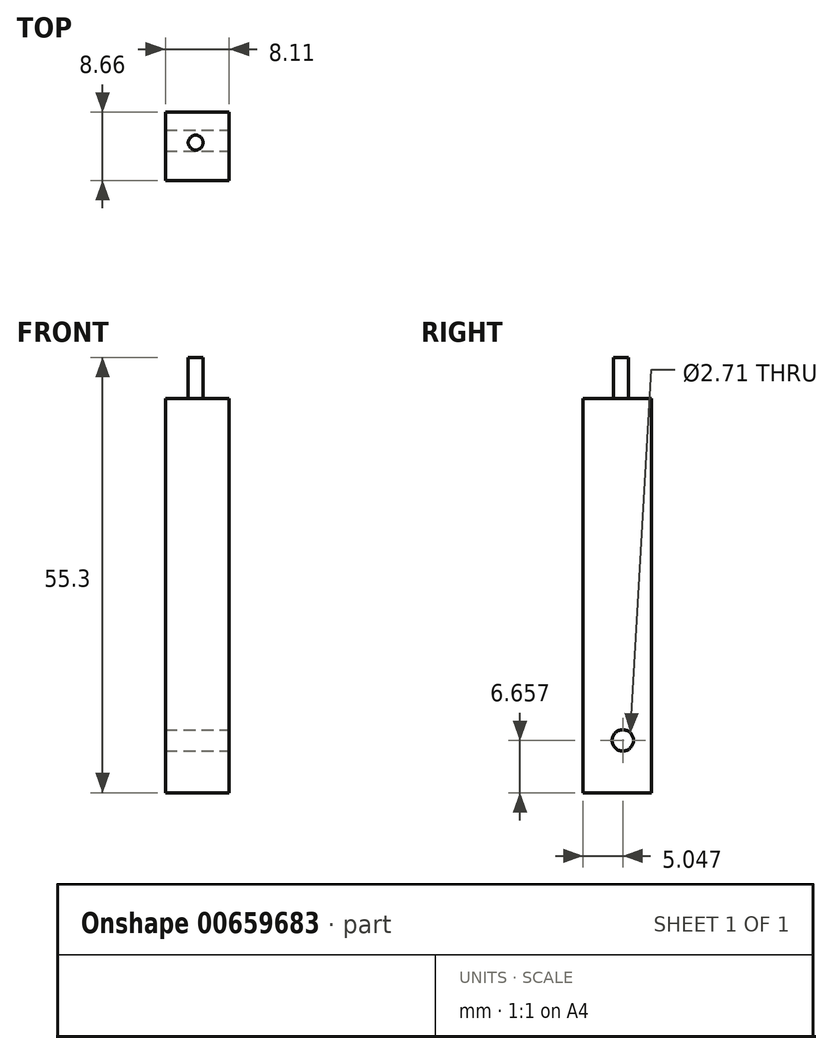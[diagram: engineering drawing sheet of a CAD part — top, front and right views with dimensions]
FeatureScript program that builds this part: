
annotation { "Feature Type Name" : "Feature", "Feature Type Description" : "" }
export const myFeature = defineFeature(function(context is Context, id is Id, definition is map)
    precondition{}
    {
        {
            var Q0;
            Q0=qCreatedBy(makeId("Top.planeOp"),FACE);
            var sketch = newSketch(context, id + "F0", { "sketchPlane" : qUnion([Q0])});
            skLineSegment(sketch, "E0.bottom", {"start": v(0, 0) * mm, "end": v(8.11, 0) * mm});
            skLineSegment(sketch, "E0.top", {"start": v(0, -8.66) * mm, "end": v(8.11, -8.66) * mm});
            skLineSegment(sketch, "E0.left", {"start": v(0, 0) * mm, "end": v(0, -8.66) * mm});
            skLineSegment(sketch, "E0.right", {"start": v(8.11, 0) * mm, "end": v(8.11, -8.66) * mm});
            skSolve(sketch);
        }
        {
            var Q0;
            Q0 = qSketchRegion(id + "F0", true);
            extrude(context, id + "F1", {"entities" : qUnion([Q0]), "depth" : 50.1 * mm, "offsetDistance" : 25 * mm});
        }
        {
            var Q0;
            Q0=makeQuery(id+"F1.opExtrude","SWEPT_FACE",FACE,{"disambiguationData":[OSD([sQuery(id+"F0.wireOp",EDGE,"E0.right")])]});
            var sketch = newSketch(context, id + "F2", { "sketchPlane" : qUnion([Q0])});
            skCircle(sketch, "E1", {"center": v(-3.61, 6.66) * mm, "radius": 1.35 * mm});
            skSolve(sketch);
        }
        {
            var Q0;
            Q0 = qSketchRegion(id + "F2", true);
            extrude(context, id + "F3", {"entities" : qUnion([Q0]), "operationType" : NewBodyOperationType.REMOVE, "oppositeDirection" : true, "depth" : 25 * mm, "offsetDistance" : 25 * mm});
        }
        {
            var Q0;
            Q0=makeQuery(id+"F1.opExtrude","CAP_FACE",FACE,{"disambiguationData":[OSD([sQuery(id+"F0.wireOp",EDGE,"E0.bottom"),sQuery(id+"F0.wireOp",EDGE,"E0.top"),sQuery(id+"F0.wireOp",EDGE,"E0.left"),sQuery(id+"F0.wireOp",EDGE,"E0.right")])],"isStart":false});
            var sketch = newSketch(context, id + "F4", { "sketchPlane" : qUnion([Q0])});
            skCircle(sketch, "E2", {"center": v(3.84, -3.86) * mm, "radius": 0.95 * mm});
            skSolve(sketch);
        }
        {
            var Q0;
            Q0 = qSketchRegion(id + "F4", true);
            extrude(context, id + "F5", {"entities" : qUnion([Q0]), "operationType" : NewBodyOperationType.ADD, "depth" : 5.2 * mm, "offsetDistance" : 25 * mm});
        }
    });
